# Revit family: HE2.zip
name_source: partatom
category: Generic Models
revit_build: Autodesk Revit 2017 (Build: 20160225_1515(x64)
units: mm (PartAtom-declared; Revit-internal decimal feet)

## family parameters
Always vertical = Yes
Can host rebar = No
Cut with Voids When Loaded = No
Host = Wall
Part Type = Normal
Room Calculation Point = No
Round Connector Dimension = Use Diameter
Shared = No

## types (1)
- HE2
    Assembly Code = D3020300
    AssetIdentifier = (Client fill)
    AssetType = (Client fill)
    Color = White - BS 4800 00A01 - 18% Gloss
    Component = HE2
    Data Sheet = http://smithsep.co.uk
    Description = HE2 complete system
    Finish = 0.7mm zinc coated steel
    Installation Guide = http://smithsep.co.uk
    InstallationDate = (Client fill)
    Keynote = (Client fill)
    Manufacturer = Smiths Enviromental Products LTD
    ManufacturerURL = http://www.smithsep.co.uk
    Model = HE2
    ModelNumber = HE2
    NBSReference = T90 Heating systems
    Revision = Rev1 - Septmber 2016
    Type Comments = (Client fill)
    URL = http://smithsep.co.uk
    Uniclass2015Reference = Ss_60_40_37_51
    Warranty Certificate = Awaiting Link
    WarrantyDescription = 5 years from date of purchase
    WarrantyStartDate = (Client fill)

## geometry (parser evidence)
native form markers: Sweep x2
no freeform markers — native parametric forms only
